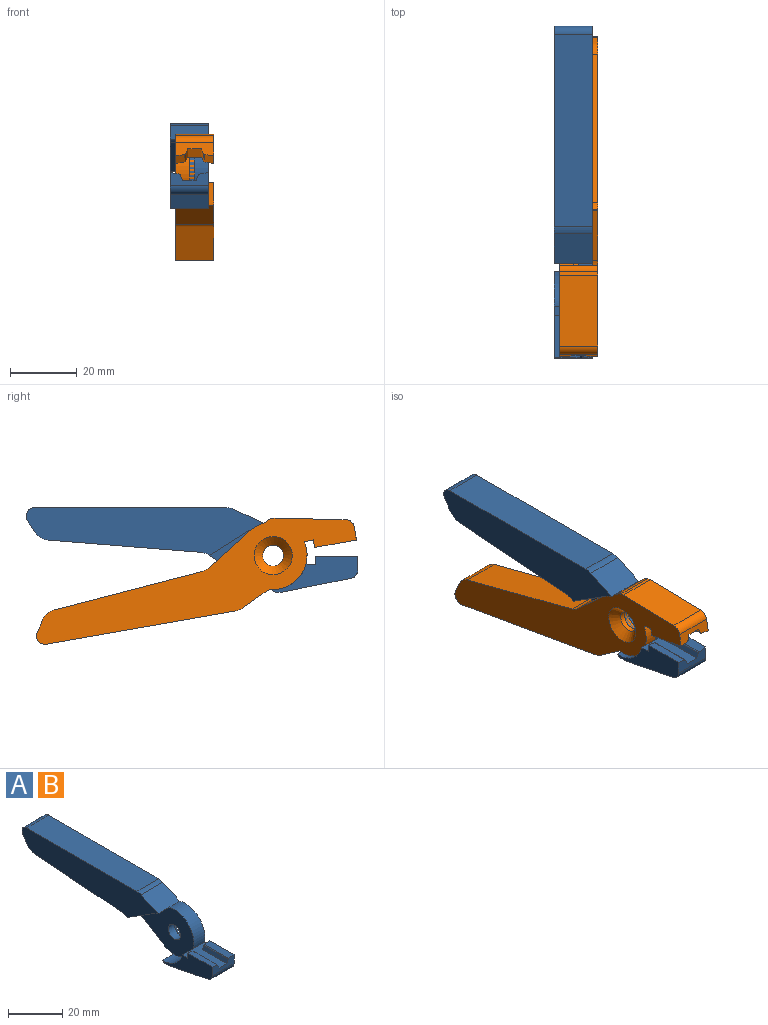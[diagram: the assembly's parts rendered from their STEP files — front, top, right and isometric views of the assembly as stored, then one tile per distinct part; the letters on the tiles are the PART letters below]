
ASSEMBLY  parts=2 mates=1
PART A: 34 faces, bbox 11.4x99.4x25.3 mm
  f0: plane 15.56x11.43mm, normal (0,0,1), area 84.3mm2, adj f1,f7,f18,f19,f22,f26,f27,f29
  f1: cylinder r=10.16mm len=13.08mm, axis (-1,0,0), area 122.8mm2, adj f0,f6,f7,f15
  f2: plane 13.38x11.43mm, normal (0,0.53,-0.85), area 92.5mm2, adj f7,f8,f9,f14,f15,f17
  f3: plane 45.76x11.43mm, normal (0,0.08,-1), area 524.7mm2, adj f7,f8,f9,f10
  f4: plane 11.43x3.51mm, normal (0,0.83,-0.56), area 48.2mm2, adj f7,f8,f10,f12
  f5: plane 57.51x11.43mm, normal (0,0,1), area 657.4mm2, adj f7,f8,f11,f12
  f6: plane 11.43x8.86mm, normal (0,-0.42,0.91), area 111.8mm2, adj f1,f7,f8,f11,f16
  f7: plane 99.39x25.33mm, normal (1,0,0), area 1153mm2, adj f0,f1,f2,f3,f4,f5,f6,f9
  f8: plane 71.07x14.33mm, normal (-1,0,0), area 738.1mm2, adj f2,f3,f4,f5,f6,f9,f10,f11
  f9: cylinder r=5.08mm len=11.43mm, axis (-1,0,0), area 28.1mm2, adj f2,f3,f7,f8
  f10: cylinder r=5.08mm len=11.43mm, axis (-1,0,0), area 52.4mm2, adj f3,f4,f7,f8
  f11: cylinder r=5.08mm len=11.43mm, axis (-1,0,0), area 25.4mm2, adj f5,f6,f7,f8
  f12: cylinder r=2.54mm len=11.43mm, axis (-1,0,0), area 62.7mm2, adj f4,f5,f7,f8
  f13: cylinder r=3.17mm len=6.35mm, axis (-1,0,0), area 63.3mm2, adj f15,f33
  f14: cylinder r=10.16mm len=5.72mm, axis (-1,0,0), area 33.3mm2, adj f2,f7,f15,f24
  f15: plane 29.18x20.32mm, normal (-1,0,0), area 351.9mm2, adj f1,f2,f13,f14,f16,f17,f18
  f16: cylinder r=10.16mm len=5.72mm, axis (1,0,0), area 15.7mm2, adj f6,f8,f15,f17
  f17: plane 13.61x8.57mm, normal (0,-0.53,-0.85), area 91.9mm2, adj f2,f8,f15,f16
  f18: cylinder r=10.16mm len=10.38mm, axis (-1,0,0), area 79.6mm2, adj f0,f15,f22,f24
  f19: plane 11.43x4.03mm, normal (0,-1,0), area 33.2mm2, adj f0,f7,f22,f23,f25,f26,f28,f29
  f20: plane 20.84x11.43mm, normal (0,-0.2,-0.98), area 243mm2, adj f7,f21,f22,f23
  f21: plane 11.43x1.19mm, normal (0,0,-1), area 13.6mm2, adj f7,f20,f22,f24
  f22: plane 25.94x10.72mm, normal (-1,0,0), area 134mm2, adj f0,f18,f19,f20,f21,f23,f24,f28
  f23: cylinder r=2.54mm len=11.43mm, axis (-1,0,0), area 39.8mm2, adj f7,f19,f20,f22
  f24: cylinder r=2.54mm len=11.43mm, axis (-1,0,0), area 24.1mm2, adj f7,f14,f18,f21,f22
  f25: plane 12.7x2.68mm, normal (-0.17,0,0.99), area 34.5mm2, adj f7,f19,f27,f32
  f26: plane 12.7x1.52mm, normal (-0.92,0,0.38), area 20.8mm2, adj f0,f19,f27,f32
  f27: plane 3.68x2.29mm, normal (0,1,0), area 6.6mm2, adj f0,f7,f25,f26,f32
  f28: plane 12.7x2.68mm, normal (0.17,0,0.99), area 34.5mm2, adj f19,f22,f30,f31
  f29: plane 12.7x1.52mm, normal (0.92,0,0.38), area 20.8mm2, adj f0,f19,f30,f31
  f30: plane 3.68x2.29mm, normal (0,1,0), area 6.6mm2, adj f0,f22,f28,f29,f31
  f31: cylinder r=0.51mm len=12.7mm, axis (0,-1,0), area 6.5mm2, adj f19,f28,f29,f30
  f32: cylinder r=0.51mm len=12.7mm, axis (0,-1,0), area 6.5mm2, adj f19,f25,f26,f27
  f33: cone r=3.17mm half-angle=45deg, axis (1,0,0), area 100.3mm2, adj f7,f13
PART B: same geometry as A
PLACE A t=(18.33,-31.42,-2.32)mm
PLACE B rot(axis=(0,-1,0.09),180deg) t=(19.92,-31.42,-2.32)mm
MATE revolute B.f1 <-> A.f1  axis (1,0,0) through (18.33,-31.42,-2.32)mm
